# Revit family: SH-5730-50W
name_source: partatom
category: Lighting Fixtures
revit_build: Autodesk Revit 2017 (Build: 20160225_1515(x64)
units: mm (PartAtom-declared; Revit-internal decimal feet)

## family parameters
Always vertical = No
Cut with Voids When Loaded = No
Light Source = No
OmniClass Number = 23.80.70.00
OmniClass Title = Lighting
Part Type = Normal
Room Calculation Point = No
Round Connector Dimension = Use Diameter
Shared = Yes
Work Plane-Based = Yes

## types (10) — shared parameters
Body Material = Aluminum
Default Elevation = 121.9 cm
Diffuser = Glass
Flicker = Free Flicker
Height = 28.1 cm
IP = IP65
Lamp = LED
Length = 31.6 cm
Manufacturer = SHOA
Model = SH-5730-50w
Protection Class = Class I
Reflector Material = Anodize material
Type medule = SMD
URL = https://www.shoaco.com
Voltage/Frequency = 230V/50HZ
Website = www.shoaco.com
Width = 4.2 cm
consumption current = 0 A
wattage = 50 W

## per-type parameters (varying)
| type | 3000K | 6500K | Blue | Body color | Color light | Green | RED | color rendering index(CRI) | color temperature |
| Sh-5730-50W(Black color-3000K-LED) | Yes | No | No | Black color |  | No | No | 80< | 3000K |
| Sh-5730-50W(Black color-6500K-LED) | No | Yes | No | Black color |  | No | No | 80< | 6500K |
| Sh-5730-50W(Black color-Blue-LED) | No | No | Yes | Black color | Blue | No | No |  |  |
| Sh-5730-50W(Black color-Green-LED) | No | No | No | Black color | Green | Yes | No |  |  |
| Sh-5730-50W(Black color-RED-LED) | No | No | No | Black color | Red | No | Yes |  |  |
| Sh-5730-50W(White color-3000K-LED) | Yes | No | No | White color |  | No | No | 80< | 3000K |
| Sh-5730-50W(White color-6500K-LED) | No | Yes | No | White color |  | No | No | 80< | 6500K |
| Sh-5730-50W(White color-Blue-LED) | No | No | Yes | White color | Blue | No | No |  |  |
| Sh-5730-50W(White color-Green-LED) | No | No | No | White color | Green | Yes | No |  |  |
| Sh-5730-50W(White color-RED-LED) | No | No | No | White color | Red | No | Yes |  |  |

## geometry (parser evidence)
native form markers: Sweep x9
no freeform markers — native parametric forms only
